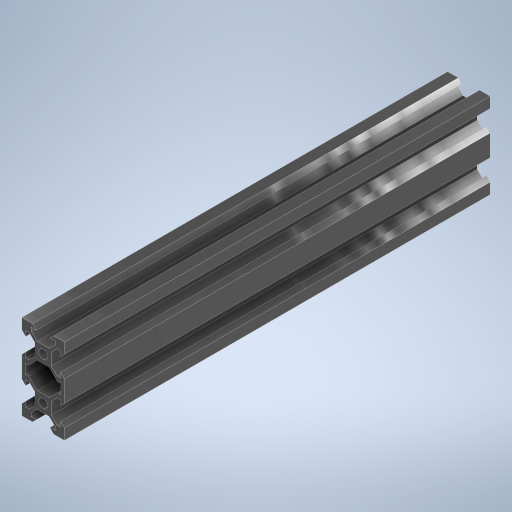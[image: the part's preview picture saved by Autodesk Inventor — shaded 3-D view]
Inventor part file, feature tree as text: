
AUTODESK INVENTOR PART (.ipt)
format: ipt  version: 2024.2 (Build 282272000, 272)  size: 415,232 bytes
history: native  units: mm
features: extrude x2, sketch x2, pattern_linear x1
ambient origin geometry x8: Origin, YZ Plane, XZ Plane, XY Plane, X Axis, Y Axis, Z Axis, Center Point
bodies: Solid1 (feature_tree)
feature tree (5):
  extrude  "Extrusion1"  Depth=10.0mm
  pattern_linear  "Rectangular Pattern1"  Spacing1=4.4mm  [1 undecoded]
  extrude  "Extrusion2"  TaperAngle=45.0deg  [1 undecoded]
  sketch  "Sketch1"  dims[d16=10.0mm d19=3.2mm]
  sketch  "Sketch2"  dims[d21=4.4mm d22=4.4mm d24=45.0deg d25=1.8mm d27=1.8mm d28=45.0deg d29=3.2mm d31=1.4mm d33=2.15mm d34=3.825mm d35=3.825mm d36=135.0deg d37=40.0mm d39=360.0deg d41=200.0mm d42=0.0mm d43=20.0mm d45=20.0mm d46=4.5mm d48=0.0mm d49=0.0mm d50=1.8mm d51=0.5mm d52=0.872665mm d53=0.5mm d54=0.872665mm]
note: 2 required parameter values undecoded (feature->parameter linkage not recoverable at this tier; creation-order binding heuristic only, values carry confidence <= 0.55)
